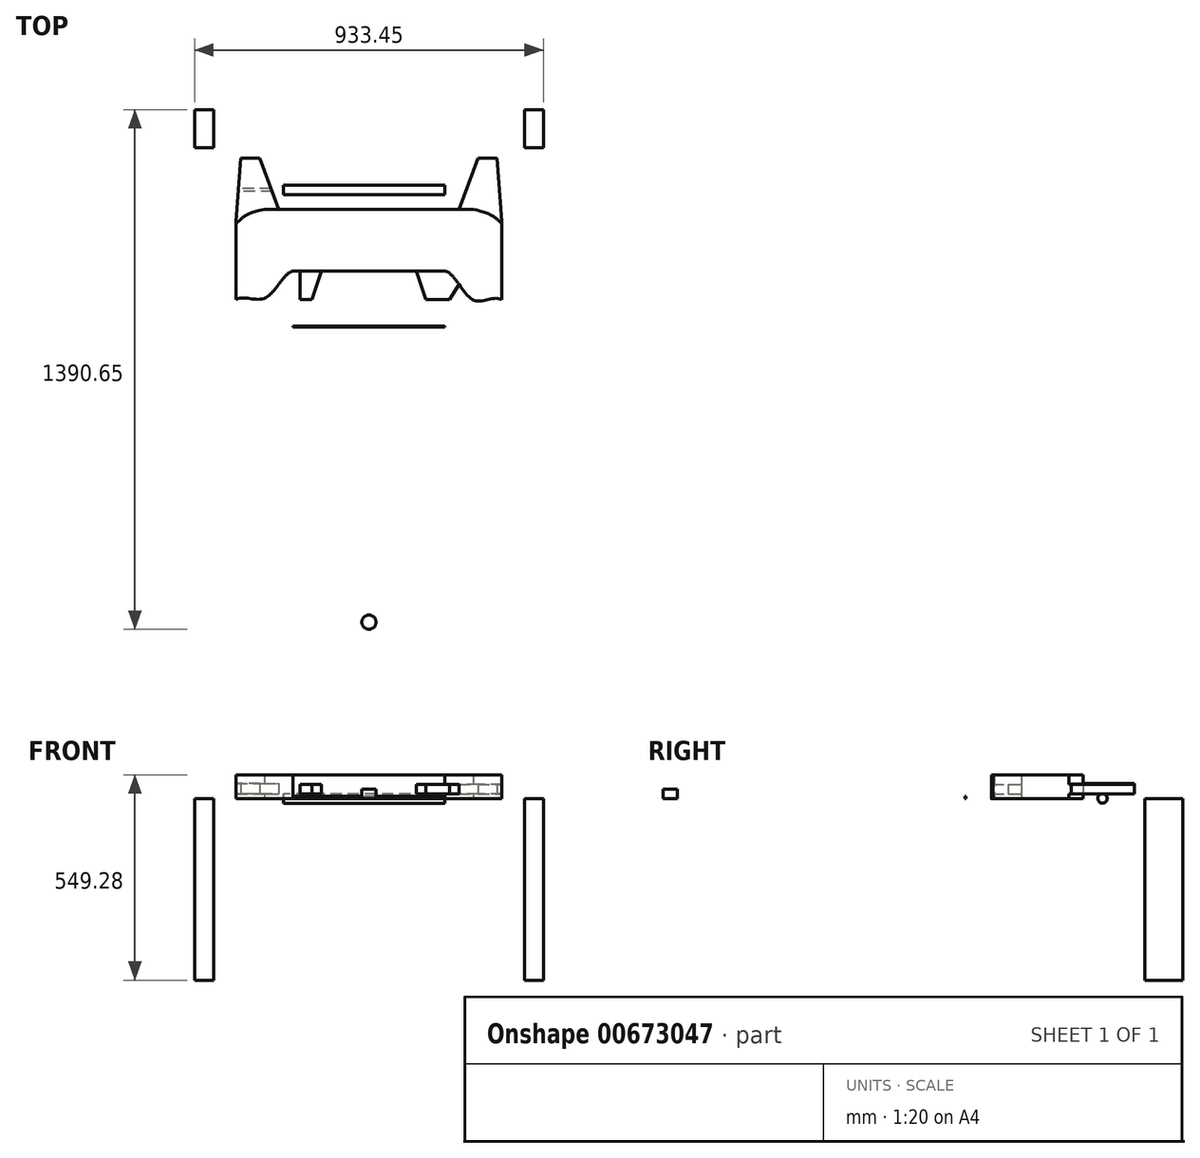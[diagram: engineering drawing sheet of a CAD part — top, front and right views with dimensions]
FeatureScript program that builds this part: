
annotation { "Feature Type Name" : "Feature", "Feature Type Description" : "" }
export const myFeature = defineFeature(function(context is Context, id is Id, definition is map)
    precondition{}
    {
        {
            var Q0;
            Q0=qCreatedBy(makeId("Top.planeOp"),FACE);
            var sketch = newSketch(context, id + "F0", { "sketchPlane" : qUnion([Q0])});
            skLineSegment(sketch, "E0", {"start": v(-203.66, -92.87) * mm, "end": v(75.74, -92.87) * mm});
            skLineSegment(sketch, "E1", {"start": v(-483.06, -92.87) * mm, "end": v(-203.66, -92.87) * mm});
            skFitSpline(sketch, "E2", {"points": [v(-559.26, -130.97) * mm, v(-532.92, -108.95) * mm, v(-483.06, -92.87) * mm], "startDerivative": vector(87.15, 83.97) * mm, "endDerivative": vector(162.07, 33.25) * mm});
            skLineSegment(sketch, "E3", {"start": v(-203.66, -257.97) * mm, "end": v(-330.66, -257.97) * mm});
            skLineSegment(sketch, "E4", {"start": v(-203.66, -257.97) * mm, "end": v(-406.86, -257.97) * mm});
            skLineSegment(sketch, "E5", {"start": v(-559.26, -283.37) * mm, "end": v(-559.26, -334.17) * mm});
            skFitSpline(sketch, "E6", {"points": [v(-559.26, -334.17) * mm, v(-480.11, -329.57) * mm, v(-406.86, -257.97) * mm], "startDerivative": vector(157.63, 76.39) * mm, "endDerivative": vector(146.98, 24.27) * mm});
            skLineSegment(sketch, "E7", {"start": v(-203.66, -257.97) * mm, "end": v(-387.8, -257.97) * mm});
            skLineSegment(sketch, "E8", {"start": v(-559.26, -283.37) * mm, "end": v(-559.26, -130.97) * mm});
            skLineSegment(sketch, "E9", {"start": v(-203.66, -92.87) * mm, "end": v(-444.96, -92.87) * mm});
            skLineSegment(sketch, "E10", {"start": v(-495.76, 44.5) * mm, "end": v(-444.96, -92.87) * mm});
            skLineSegment(sketch, "E11", {"start": v(-495.76, 44.5) * mm, "end": v(-546.26, 44.5) * mm});
            skLineSegment(sketch, "E12", {"start": v(-546.26, 44.5) * mm, "end": v(-559.26, -124.58) * mm});
            skFitSpline(sketch, "E13.MirrorCS", {"points": [v(151.94, -334.17) * mm, v(75.96, -335.3) * mm, v(-0.46, -257.97) * mm], "startDerivative": vector(-157.63, 76.39) * mm, "endDerivative": vector(-146.98, 24.27) * mm});
            skLineSegment(sketch, "E14.MirrorCS", {"start": v(151.94, -283.37) * mm, "end": v(151.94, -334.17) * mm});
            skLineSegment(sketch, "E15.MirrorCS", {"start": v(151.94, -283.37) * mm, "end": v(151.94, -130.97) * mm});
            skLineSegment(sketch, "E16.MirrorCS", {"start": v(138.95, 44.5) * mm, "end": v(151.94, -124.58) * mm});
            skLineSegment(sketch, "E17.MirrorCS", {"start": v(88.44, 44.5) * mm, "end": v(138.95, 44.5) * mm});
            skLineSegment(sketch, "E18.MirrorCS", {"start": v(88.44, 44.5) * mm, "end": v(37.64, -92.87) * mm});
            skFitSpline(sketch, "E19.MirrorCS", {"points": [v(151.94, -130.97) * mm, v(130.55, -112.5) * mm, v(75.74, -92.87) * mm], "startDerivative": vector(-87.15, 83.97) * mm, "endDerivative": vector(-162.07, 33.25) * mm});
            skLineSegment(sketch, "E20", {"start": v(-203.66, -257.97) * mm, "end": v(-63.96, -257.97) * mm});
            skLineSegment(sketch, "E21", {"start": v(-0.46, -257.97) * mm, "end": v(-63.96, -257.97) * mm});
            skLineSegment(sketch, "E22", {"start": v(-559.26, -124.58) * mm, "end": v(-559.26, -130.97) * mm});
            skLineSegment(sketch, "E23", {"start": v(151.94, -124.58) * mm, "end": v(151.94, -130.97) * mm});
            skLineSegment(sketch, "E24", {"start": v(-203.1, -79.52) * mm, "end": v(0.1, -79.52) * mm});
            skLineSegment(sketch, "E25", {"start": v(-203.1, -79.52) * mm, "end": v(-406.3, -79.52) * mm});
            skLineSegment(sketch, "E26", {"start": v(-203.66, -257.97) * mm, "end": v(-203.66, -1197.77) * mm});
            skCircle(sketch, "E27", {"center": v(-203.66, -1197.77) * mm, "radius": 19.05 * mm});
            skLineSegment(sketch, "E28", {"start": v(-203.66, -257.97) * mm, "end": v(-203.66, -405.62) * mm});
            skLineSegment(sketch, "E29", {"start": v(-203.66, -405.62) * mm, "end": v(-0.46, -405.62) * mm});
            skLineSegment(sketch, "E30", {"start": v(-0.46, -405.62) * mm, "end": v(-0.46, -408.16) * mm});
            skLineSegment(sketch, "E31", {"start": v(-0.46, -408.16) * mm, "end": v(-406.86, -408.16) * mm});
            skLineSegment(sketch, "E32", {"start": v(-406.86, -408.16) * mm, "end": v(-406.86, -405.62) * mm});
            skLineSegment(sketch, "E33", {"start": v(-406.86, -405.62) * mm, "end": v(-203.66, -405.62) * mm});
            skLineSegment(sketch, "E34", {"start": v(-387.8, -257.97) * mm, "end": v(-387.8, -334.17) * mm});
            skLineSegment(sketch, "E35", {"start": v(-387.8, -334.17) * mm, "end": v(-356.06, -334.17) * mm});
            skLineSegment(sketch, "E36", {"start": v(-356.06, -334.17) * mm, "end": v(-330.66, -257.97) * mm});
            skLineSegment(sketch, "E37", {"start": v(-387.8, -334.17) * mm, "end": v(-419.56, -334.17) * mm});
            skLineSegment(sketch, "E38", {"start": v(-419.56, -334.17) * mm, "end": v(-444.96, -293.04) * mm});
            skLineSegment(sketch, "E39.MirrorCS", {"start": v(12.24, -334.17) * mm, "end": v(37.64, -293.04) * mm});
            skLineSegment(sketch, "E40.MirrorCS", {"start": v(-19.5, -257.97) * mm, "end": v(-19.5, -334.17) * mm});
            skLineSegment(sketch, "E41.MirrorCS", {"start": v(-51.26, -334.17) * mm, "end": v(-76.66, -257.97) * mm});
            skLineSegment(sketch, "E42.MirrorCS", {"start": v(-19.5, -334.17) * mm, "end": v(12.24, -334.17) * mm});
            skLineSegment(sketch, "E43.MirrorCS", {"start": v(-19.5, -334.17) * mm, "end": v(-51.26, -334.17) * mm});
            skLineSegment(sketch, "E44", {"start": v(-203.66, -92.87) * mm, "end": v(-203.66, 72.23) * mm});
            skLineSegment(sketch, "E45", {"start": v(-203.66, 72.23) * mm, "end": v(263.07, 72.23) * mm});
            skLineSegment(sketch, "E46", {"start": v(263.07, 72.23) * mm, "end": v(263.07, 173.83) * mm});
            skLineSegment(sketch, "E47", {"start": v(263.07, 173.83) * mm, "end": v(-670.38, 173.83) * mm});
            skLineSegment(sketch, "E48", {"start": v(-670.38, 173.83) * mm, "end": v(-670.38, 72.23) * mm});
            skLineSegment(sketch, "E49", {"start": v(-670.38, 72.23) * mm, "end": v(-203.66, 72.23) * mm});
            skSolve(sketch);
        }
        {
            var Q0;
            Q0=makeQuery(id+"F0.imprint","IMPRINT",FACE,{"disambiguationData":[TD([[makeQuery(id+"F0.imprint","IMPRINT",EDGE,{"derivedFrom":sQuery(id+"F0.wireOp",EDGE,"E1")}),-1.0]])]});
            extrude(context, id + "F1", {"entities" : qUnion([Q0]), "depth" : 63.5 * mm, "offsetDistance" : 25.4 * mm});
        }
        {
            var Q0;
            {var subQ2=sQuery(id+"F0.wireOp",EDGE,"E4");Q0=makeQuery(id+"F0.imprint","IMPRINT",FACE,{"disambiguationData":[TD([[makeQuery(id+"F0.imprint","IMPRINT",EDGE,{"derivedFrom":subQ2}),1.0]])]});}
            var Q1;
            {var subQ0=sQuery(id+"F0.wireOp",EDGE,"E34");Q1=makeQuery(id+"F0.imprint","IMPRINT",FACE,{"disambiguationData":[TD([[makeQuery(id+"F0.imprint","IMPRINT",EDGE,{"derivedFrom":subQ0}),1.0]])]});}
            var Q2;
            {var subQ0=sQuery(id+"F0.wireOp",EDGE,"E40.MirrorCS");Q2=makeQuery(id+"F0.imprint","IMPRINT",FACE,{"disambiguationData":[TD([[makeQuery(id+"F0.imprint","IMPRINT",EDGE,{"derivedFrom":subQ0}),-1.0]])]});}
            var Q3;
            {var subQ0=sQuery(id+"F0.wireOp",EDGE,"E40.MirrorCS");Q3=makeQuery(id+"F0.imprint","IMPRINT",FACE,{"disambiguationData":[TD([[makeQuery(id+"F0.imprint","IMPRINT",EDGE,{"derivedFrom":subQ0}),1.0]])]});}
            extrude(context, id + "F2", {"entities" : qUnion([Q0, Q1, Q2, Q3]), "operationType" : NewBodyOperationType.ADD, "depth" : 38.1 * mm, "offsetDistance" : 25.4 * mm});
        }
        {
            var Q0;
            {var subQ2=sQuery(id+"F0.wireOp",EDGE,"E4");Q0=makeQuery(id+"F0.imprint","IMPRINT",FACE,{"disambiguationData":[TD([[makeQuery(id+"F0.imprint","IMPRINT",EDGE,{"derivedFrom":subQ2}),1.0]])]});}
            var Q1;
            {var subQ0=sQuery(id+"F0.wireOp",EDGE,"E34");Q1=makeQuery(id+"F0.imprint","IMPRINT",FACE,{"disambiguationData":[TD([[makeQuery(id+"F0.imprint","IMPRINT",EDGE,{"derivedFrom":subQ0}),1.0]])]});}
            var Q2;
            {var subQ0=sQuery(id+"F0.wireOp",EDGE,"E40.MirrorCS");Q2=makeQuery(id+"F0.imprint","IMPRINT",FACE,{"disambiguationData":[TD([[makeQuery(id+"F0.imprint","IMPRINT",EDGE,{"derivedFrom":subQ0}),-1.0]])]});}
            var Q3;
            {var subQ0=sQuery(id+"F0.wireOp",EDGE,"E40.MirrorCS");Q3=makeQuery(id+"F0.imprint","IMPRINT",FACE,{"disambiguationData":[TD([[makeQuery(id+"F0.imprint","IMPRINT",EDGE,{"derivedFrom":subQ0}),1.0]])]});}
            extrude(context, id + "F3", {"entities" : qUnion([Q0, Q1, Q2, Q3]), "operationType" : NewBodyOperationType.REMOVE, "depth" : 12.7 * mm, "offsetDistance" : 25.4 * mm});
        }
        {
            var Q0;
            Q0=makeQuery(id+"F0.imprint","IMPRINT",FACE,{"disambiguationData":[TD([[makeQuery(id+"F0.imprint","IMPRINT",EDGE,{"derivedFrom":sQuery(id+"F0.wireOp",EDGE,"E1")}),1.0]])]});
            extrude(context, id + "F4", {"entities" : qUnion([Q0]), "operationType" : NewBodyOperationType.ADD, "depth" : 40.64 * mm, "offsetDistance" : 25.4 * mm});
        }
        {
            var Q0;
            Q0=makeQuery(id+"F0.imprint","IMPRINT",FACE,{"disambiguationData":[TD([[makeQuery(id+"F0.imprint","IMPRINT",EDGE,{"derivedFrom":sQuery(id+"F0.wireOp",EDGE,"E1")}),1.0]])]});
            extrude(context, id + "F5", {"entities" : qUnion([Q0]), "operationType" : NewBodyOperationType.REMOVE, "depth" : 12.7 * mm, "offsetDistance" : 25.4 * mm});
        }
        {
            var Q0;
            Q0=makeQuery(id+"F0.imprint","IMPRINT",FACE,{"disambiguationData":[TD([[makeQuery(id+"F0.imprint","IMPRINT",EDGE,{"derivedFrom":sQuery(id+"F0.wireOp",EDGE,"E16.MirrorCS")}),-1.0]])]});
            extrude(context, id + "F6", {"entities" : qUnion([Q0]), "operationType" : NewBodyOperationType.ADD, "depth" : 38.1 * mm, "offsetDistance" : 25.4 * mm});
        }
        {
            var Q0;
            Q0=makeQuery(id+"F0.imprint","IMPRINT",FACE,{"disambiguationData":[TD([[makeQuery(id+"F0.imprint","IMPRINT",EDGE,{"derivedFrom":sQuery(id+"F0.wireOp",EDGE,"E16.MirrorCS")}),-1.0]])]});
            extrude(context, id + "F7", {"entities" : qUnion([Q0]), "operationType" : NewBodyOperationType.REMOVE, "depth" : 12.7 * mm, "offsetDistance" : 25.4 * mm});
        }
        {
            var Q0;
            Q0=makeQuery(id+"F1.opExtrude","SWEPT_FACE",FACE,{"disambiguationData":[OSD([sQuery(id+"F0.wireOp",EDGE,"E8")])]});
            var sketch = newSketch(context, id + "F8", { "sketchPlane" : qUnion([Q0])});
            skCircle(sketch, "E50", {"center": v(40.67, 0.68) * mm, "radius": 12.7 * mm});
            skSolve(sketch);
        }
        {
            var Q0;
            Q0 = qSketchRegion(id + "F8", true);
            extrude(context, id + "F9", {"entities" : qUnion([Q0]), "operationType" : NewBodyOperationType.ADD, "oppositeDirection" : true, "depth" : 558.8 * mm, "offsetDistance" : 25.4 * mm});
        }
        {
            var Q0;
            Q0=makeQuery(id+"F9.opExtrude","CAP_FACE",FACE,{"disambiguationData":[OSD([sQuery(id+"F8.wireOp",EDGE,"E50")])],"isStart":true});
            extrude(context, id + "F10", {"entities" : qUnion([Q0]), "operationType" : NewBodyOperationType.REMOVE, "oppositeDirection" : true, "depth" : 127 * mm, "offsetDistance" : 25.4 * mm});
        }
        {
            var Q0;
            Q0=makeQuery(id+"F0.imprint","IMPRINT",FACE,{"disambiguationData":[TD([[makeQuery(id+"F0.imprint","IMPRINT",EDGE,{"derivedFrom":sQuery(id+"F0.wireOp",EDGE,"E27")}),1.0]])]});
            extrude(context, id + "F11", {"entities" : qUnion([Q0]), "depth" : 25.4 * mm, "offsetDistance" : 25.4 * mm});
        }
        {
            var Q0;
            {var subQ4=sQuery(id+"F0.wireOp",EDGE,"E32");Q0=makeQuery(id+"F0.imprint","IMPRINT",FACE,{"disambiguationData":[TD([[makeQuery(id+"F0.imprint","IMPRINT",EDGE,{"derivedFrom":subQ4}),-1.0]])]});}
            var Q1;
            {var subQ0=sQuery(id+"F0.wireOp",EDGE,"E29");Q1=makeQuery(id+"F0.imprint","IMPRINT",FACE,{"disambiguationData":[TD([[makeQuery(id+"F0.imprint","IMPRINT",EDGE,{"derivedFrom":subQ0}),-1.0]])]});}
            extrude(context, id + "F12", {"entities" : qUnion([Q0, Q1]), "depth" : 6.35 * mm, "offsetDistance" : 25.4 * mm});
        }
        {
            var Q0;
            Q0=makeQuery(id+"F0.imprint","IMPRINT",FACE,{"disambiguationData":[TD([[makeQuery(id+"F0.imprint","IMPRINT",EDGE,{"derivedFrom":sQuery(id+"F0.wireOp",EDGE,"E45")}),1.0]])]});
            extrude(context, id + "F13", {"entities" : qUnion([Q0]), "oppositeDirection" : true, "depth" : 485.77 * mm, "offsetDistance" : 25.4 * mm});
        }
        {
            var Q0;
            Q0=makeQuery(id+"F13.opExtrude","SWEPT_FACE",FACE,{"disambiguationData":[OSD([sQuery(id+"F0.wireOp",EDGE,"E47")])]});
            var sketch = newSketch(context, id + "F14", { "sketchPlane" : qUnion([Q0])});
            skLineSegment(sketch, "E51", {"start": v(670.38, -485.78) * mm, "end": v(619.58, -485.78) * mm});
            skLineSegment(sketch, "E52", {"start": v(619.58, -485.78) * mm, "end": v(619.58, 0) * mm});
            skLineSegment(sketch, "E53", {"start": v(-263.07, -485.78) * mm, "end": v(-212.27, -485.78) * mm});
            skLineSegment(sketch, "E54", {"start": v(-212.27, -485.78) * mm, "end": v(-212.27, 0) * mm});
            skLineSegment(sketch, "E55", {"start": v(619.58, 0) * mm, "end": v(619.58, -3.18) * mm});
            skLineSegment(sketch, "E56", {"start": v(619.58, -3.18) * mm, "end": v(-212.27, -3.18) * mm});
            skLineSegment(sketch, "E57", {"start": v(619.58, -485.78) * mm, "end": v(619.58, -441.33) * mm});
            skLineSegment(sketch, "E58", {"start": v(619.58, -441.33) * mm, "end": v(-212.27, -441.33) * mm});
            skLineSegment(sketch, "E59", {"start": v(-212.27, -441.33) * mm, "end": v(-212.27, -485.78) * mm});
            skSolve(sketch);
        }
        {
            var Q0;
            Q0=makeQuery(id+"F14.imprint","IMPRINT",FACE,{"disambiguationData":[TD([[makeQuery(id+"F14.imprint","IMPRINT",EDGE,{"derivedFrom":sQuery(id+"F14.wireOp",EDGE,"E52")}),1.0]])]});
            extrude(context, id + "F15", {"entities" : qUnion([Q0]), "operationType" : NewBodyOperationType.REMOVE, "oppositeDirection" : true, "depth" : 101.6 * mm, "offsetDistance" : 25.4 * mm});
        }
        {
            var Q0;
            Q0=makeQuery(id+"F13.opExtrude","SWEPT_FACE",FACE,{"disambiguationData":[OSD([sQuery(id+"F0.wireOp",EDGE,"E45"),sQuery(id+"F0.wireOp",EDGE,"E49")])]});
            var sketch = newSketch(context, id + "F16", { "sketchPlane" : qUnion([Q0])});
            skLineSegment(sketch, "E60", {"start": v(-619.58, -441.33) * mm, "end": v(-619.58, -479.43) * mm});
            skLineSegment(sketch, "E61", {"start": v(-619.58, -479.43) * mm, "end": v(212.27, -479.43) * mm});
            skLineSegment(sketch, "E62", {"start": v(212.27, -479.43) * mm, "end": v(212.27, -441.33) * mm});
            skLineSegment(sketch, "E63", {"start": v(212.27, -441.33) * mm, "end": v(-619.58, -441.33) * mm});
            skSolve(sketch);
        }
        {
            var Q0;
            Q0 = qSketchRegion(id + "F16", true);
            extrude(context, id + "F17", {"entities" : qUnion([Q0]), "operationType" : NewBodyOperationType.REMOVE, "oppositeDirection" : true, "depth" : 97.16 * mm, "offsetDistance" : 25.4 * mm});
        }
    });
